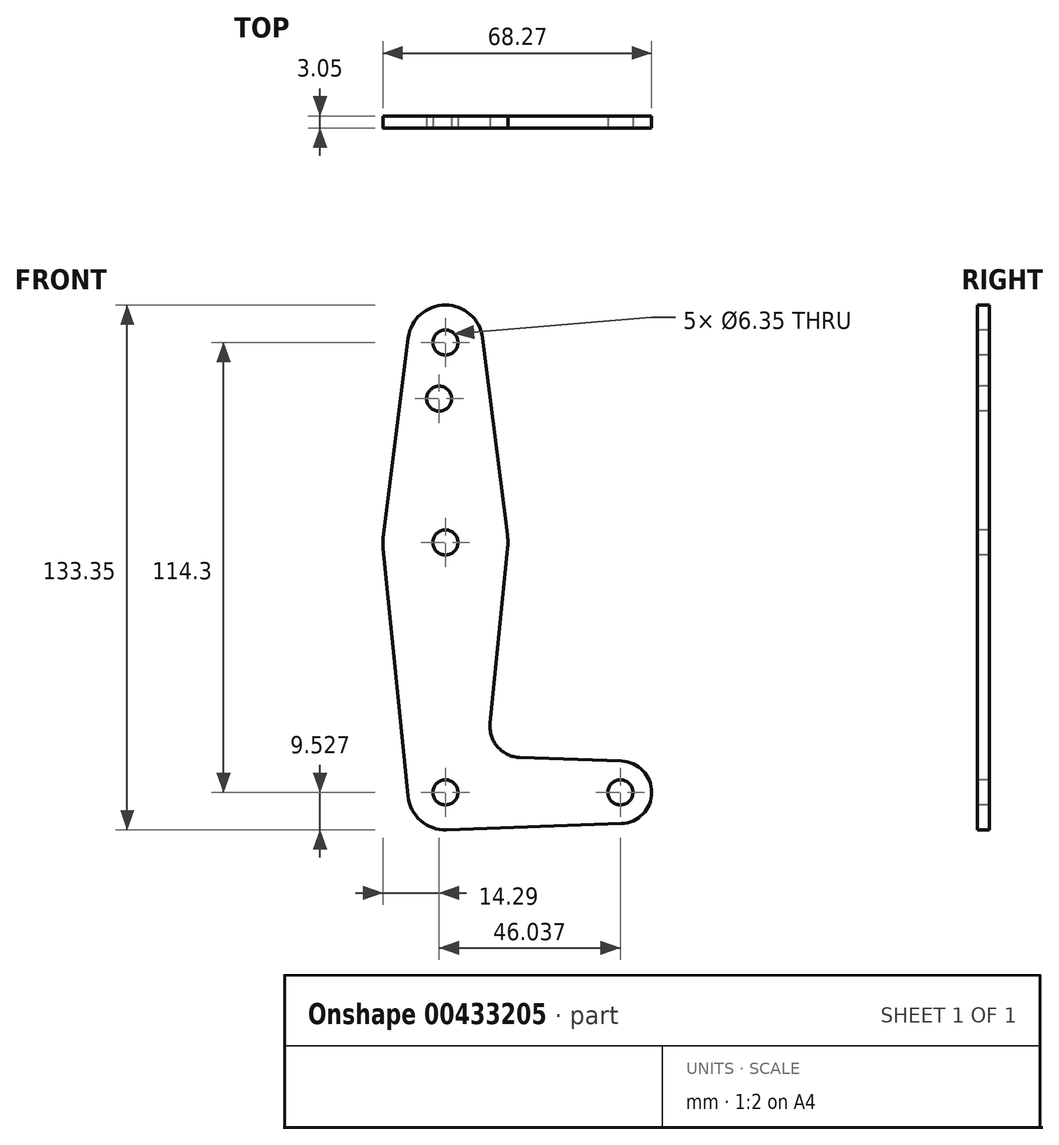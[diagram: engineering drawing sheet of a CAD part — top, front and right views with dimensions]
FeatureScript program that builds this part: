
annotation { "Feature Type Name" : "Feature", "Feature Type Description" : "" }
export const myFeature = defineFeature(function(context is Context, id is Id, definition is map)
    precondition{}
    {
        {
            var Q0;
            Q0=qCreatedBy(makeId("Front.planeOp"),FACE);
            var sketch = newSketch(context, id + "F0", { "sketchPlane" : qUnion([Q0])});
            skCircle(sketch, "E0", {"center": v(88.84, 439.34) * mm, "radius": 9.53 * mm});
            skCircle(sketch, "E1", {"center": v(88.84, 388.54) * mm, "radius": 15.88 * mm});
            skCircle(sketch, "E2", {"center": v(88.84, 325.04) * mm, "radius": 9.53 * mm});
            skCircle(sketch, "E3", {"center": v(133.29, 325.04) * mm, "radius": 7.94 * mm});
            skLineSegment(sketch, "E4", {"start": v(88.84, 439.34) * mm, "end": v(88.84, 388.54) * mm, "construction": true});
            skLineSegment(sketch, "E5", {"start": v(88.84, 388.54) * mm, "end": v(88.84, 325.04) * mm, "construction": true});
            skLineSegment(sketch, "E6", {"start": v(88.84, 325.04) * mm, "end": v(133.29, 325.04) * mm, "construction": true});
            skLineSegment(sketch, "E7", {"start": v(98.29, 440.53) * mm, "end": v(104.59, 390.52) * mm});
            skLineSegment(sketch, "E8", {"start": v(79.39, 440.53) * mm, "end": v(73.09, 390.52) * mm});
            skLineSegment(sketch, "E9", {"start": v(104.63, 386.95) * mm, "end": v(100.18, 342.63) * mm});
            skLineSegment(sketch, "E10", {"start": v(73.04, 386.95) * mm, "end": v(79.36, 324.08) * mm});
            skLineSegment(sketch, "E11", {"start": v(89.18, 315.52) * mm, "end": v(133.57, 317.1) * mm});
            skLineSegment(sketch, "E12", {"start": v(107.8, 333.9) * mm, "end": v(133.57, 332.97) * mm});
            skCircle(sketch, "E13", {"center": v(88.84, 439.34) * mm, "radius": 3.18 * mm});
            skCircle(sketch, "E14", {"center": v(88.84, 388.54) * mm, "radius": 3.18 * mm});
            skCircle(sketch, "E15", {"center": v(88.84, 325.04) * mm, "radius": 3.18 * mm});
            skCircle(sketch, "E16", {"center": v(133.29, 325.04) * mm, "radius": 3.18 * mm});
            skCircle(sketch, "E17", {"center": v(87.25, 425.06) * mm, "radius": 3.18 * mm});
            skArc(sketch, "E18.filletArc", {"start": v(100.18, 342.63) * mm, "mid": v(102.1, 336.6) * mm, "end": v(107.8, 333.9) * mm});
            skSolve(sketch);
        }
        {
            var Q0;
            Q0 = qSketchRegion(id + "F0", true);
            extrude(context, id + "F1", {"entities" : qUnion([Q0]), "oppositeDirection" : true, "depth" : 3.05 * mm});
        }
    });
